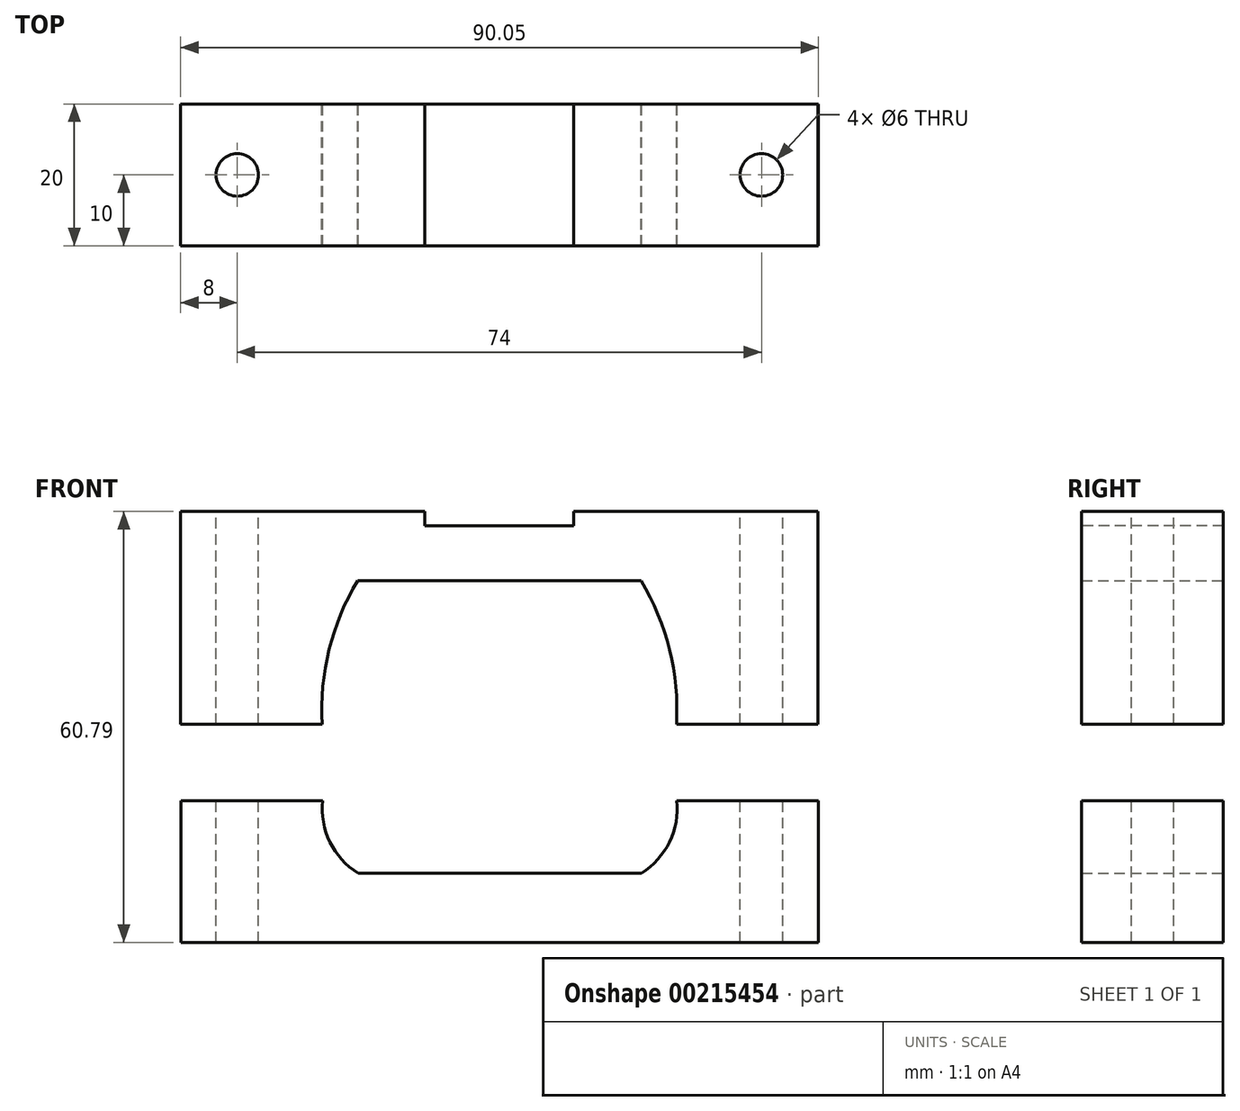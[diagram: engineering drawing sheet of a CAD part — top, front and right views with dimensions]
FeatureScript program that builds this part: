
annotation { "Feature Type Name" : "Feature", "Feature Type Description" : "" }
export const myFeature = defineFeature(function(context is Context, id is Id, definition is map)
    precondition{}
    {
        {
            var Q0;
            Q0=qCreatedBy(makeId("Front.planeOp"),FACE);
            var sketch = newSketch(context, id + "F0", { "sketchPlane" : qUnion([Q0])});
            skLineSegment(sketch, "E0", {"start": v(-45, 0) * mm, "end": v(45, 0) * mm});
            skLineSegment(sketch, "E1", {"start": v(-45, 0) * mm, "end": v(-45, -30) * mm});
            skLineSegment(sketch, "E2", {"start": v(45, 0) * mm, "end": v(45, -30) * mm});
            skLineSegment(sketch, "E3", {"start": v(-20, -9.77) * mm, "end": v(20, -9.77) * mm});
            skLineSegment(sketch, "E4", {"start": v(-45, -30) * mm, "end": v(-25, -30) * mm});
            skLineSegment(sketch, "E5", {"start": v(45, -30) * mm, "end": v(25, -30) * mm});
            skArc(sketch, "E6", {"start": v(-20, -9.77) * mm, "mid": v(-24.04, -19.5) * mm, "end": v(-25, -30) * mm});
            skArc(sketch, "E7", {"start": v(25, -30) * mm, "mid": v(24.04, -19.5) * mm, "end": v(20, -9.77) * mm});
            skSolve(sketch);
        }
        {
            var Q0;
            Q0 = qSketchRegion(id + "F0", true);
            extrude(context, id + "F1", {"entities" : qUnion([Q0]), "depth" : 20 * mm});
        }
        {
            var Q0;
            Q0=qCreatedBy(makeId("Front.planeOp"),FACE);
            var sketch = newSketch(context, id + "F2", { "sketchPlane" : qUnion([Q0])});
            skLineSegment(sketch, "E8", {"start": v(45.05, -60.8) * mm, "end": v(-44.95, -60.8) * mm});
            skLineSegment(sketch, "E9", {"start": v(20.05, -51.02) * mm, "end": v(-19.95, -51.02) * mm});
            skLineSegment(sketch, "E10", {"start": v(-44.95, -60.8) * mm, "end": v(-44.95, -40.8) * mm});
            skLineSegment(sketch, "E11", {"start": v(45.05, -60.8) * mm, "end": v(45.05, -40.8) * mm});
            skLineSegment(sketch, "E12", {"start": v(-44.95, -40.8) * mm, "end": v(-24.95, -40.8) * mm});
            skLineSegment(sketch, "E13", {"start": v(45.05, -40.8) * mm, "end": v(25.05, -40.8) * mm});
            skArc(sketch, "E14", {"start": v(-24.95, -40.8) * mm, "mid": v(-23.91, -46.63) * mm, "end": v(-19.95, -51.02) * mm});
            skArc(sketch, "E15", {"start": v(20.05, -51.02) * mm, "mid": v(24.02, -46.63) * mm, "end": v(25.05, -40.8) * mm});
            skSolve(sketch);
        }
        {
            var Q0;
            Q0 = qSketchRegion(id + "F2", true);
            extrude(context, id + "F3", {"entities" : qUnion([Q0]), "depth" : 20 * mm});
        }
        {
            var Q0;
            Q0=qCreatedBy(makeId("Top.planeOp"),FACE);
            var sketch = newSketch(context, id + "F4", { "sketchPlane" : qUnion([Q0])});
            skCircle(sketch, "E16", {"center": v(-37, -10) * mm, "radius": 3 * mm});
            skCircle(sketch, "E17", {"center": v(37, -10) * mm, "radius": 3 * mm});
            skSolve(sketch);
        }
        {
            var Q0;
            Q0=makeQuery(id+"F4.imprint","IMPRINT",FACE,{"disambiguationData":[TD([[makeQuery(id+"F4.imprint","IMPRINT",EDGE,{"derivedFrom":sQuery(id+"F4.wireOp",EDGE,"E16")}),1.0]])]});
            var Q1;
            Q1=makeQuery(id+"F4.imprint","IMPRINT",FACE,{"disambiguationData":[TD([[makeQuery(id+"F4.imprint","IMPRINT",EDGE,{"derivedFrom":sQuery(id+"F4.wireOp",EDGE,"E17")}),1.0]])]});
            var Q2;
            Q2=sQuery(id+"F4.wireOp",EDGE,"E16");
            var Q3;
            Q3=sQuery(id+"F4.wireOp",EDGE,"E17");
            extrude(context, id + "F5", {"entities" : qUnion([Q0, Q1]), "operationType" : NewBodyOperationType.REMOVE, "surfaceEntities" : qUnion([Q2, Q3]), "oppositeDirection" : true, "depth" : 150 * mm});
        }
        {
            var Q0;
            Q0=qCreatedBy(makeId("Top.planeOp"),FACE);
            var sketch = newSketch(context, id + "F6", { "sketchPlane" : qUnion([Q0])});
            skLineSegment(sketch, "E18.bottom", {"start": v(-10.5, 5.87) * mm, "end": v(10.5, 5.87) * mm});
            skLineSegment(sketch, "E18.top", {"start": v(-10.5, -24.13) * mm, "end": v(10.5, -24.13) * mm});
            skLineSegment(sketch, "E18.left", {"start": v(-10.5, 5.87) * mm, "end": v(-10.5, -24.13) * mm});
            skLineSegment(sketch, "E18.right", {"start": v(10.5, 5.87) * mm, "end": v(10.5, -24.13) * mm});
            skSolve(sketch);
        }
        {
            var Q0;
            Q0 = qSketchRegion(id + "F6", true);
            extrude(context, id + "F7", {"entities" : qUnion([Q0]), "operationType" : NewBodyOperationType.REMOVE, "oppositeDirection" : true, "depth" : 2 * mm});
        }
    });
